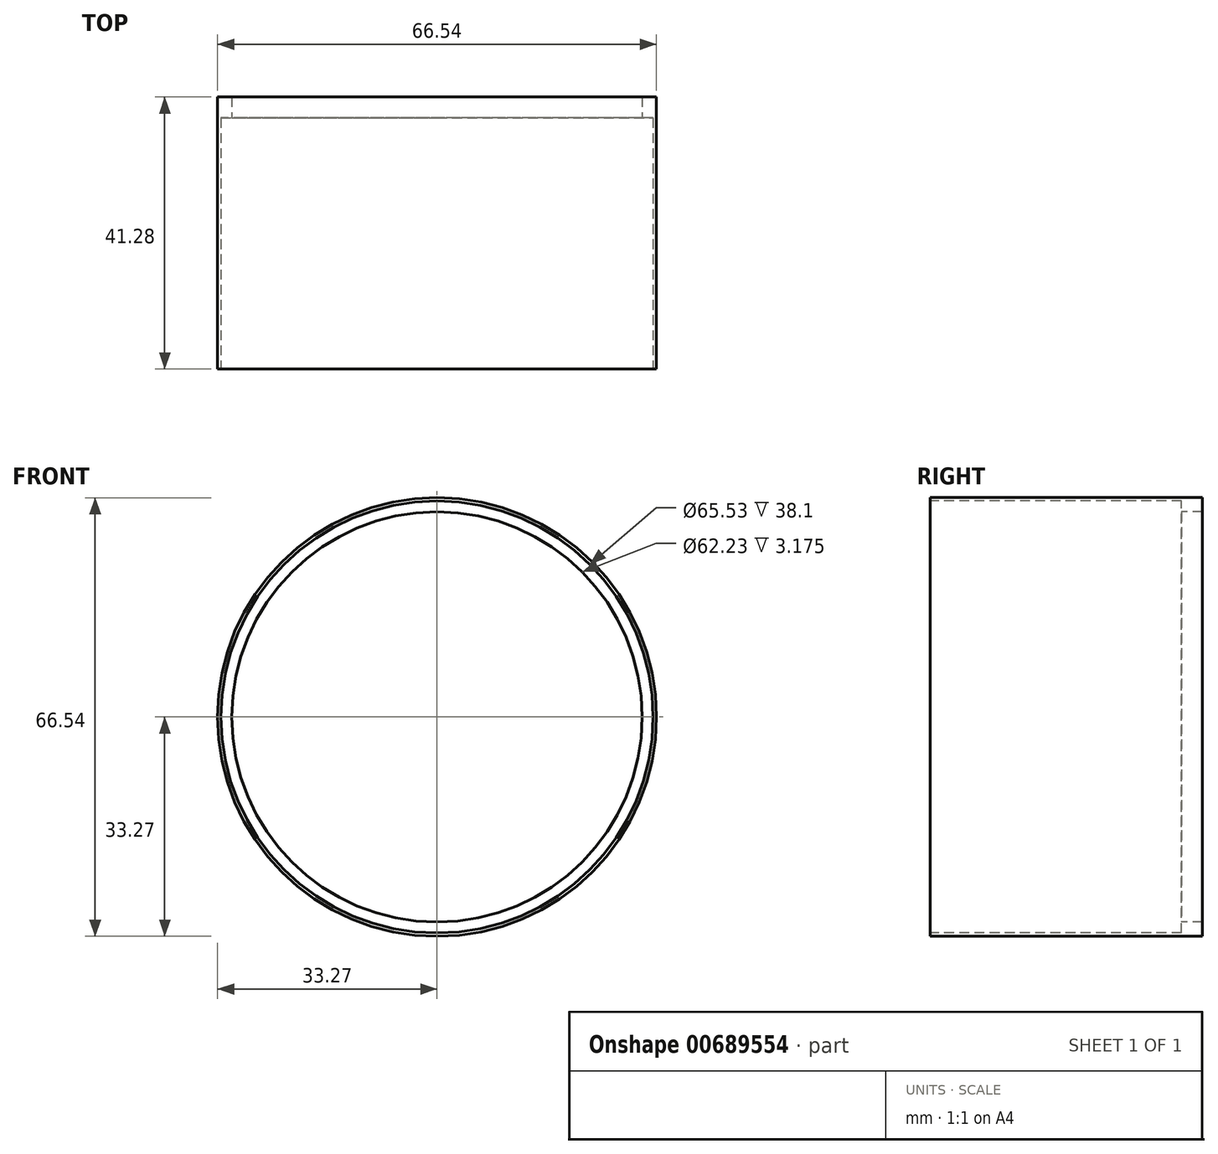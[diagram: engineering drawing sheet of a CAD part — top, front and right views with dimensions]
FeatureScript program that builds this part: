
annotation { "Feature Type Name" : "Feature", "Feature Type Description" : "" }
export const myFeature = defineFeature(function(context is Context, id is Id, definition is map)
    precondition{}
    {
        {
            var Q0;
            Q0=qCreatedBy(makeId("Front.planeOp"),FACE);
            var sketch = newSketch(context, id + "F0", { "sketchPlane" : qUnion([Q0])});
            skCircle(sketch, "E0", {"center": v(0, 0) * mm, "radius": 32.77 * mm});
            skCircle(sketch, "E1", {"center": v(0, 0) * mm, "radius": 33.27 * mm});
            skSolve(sketch);
        }
        {
            var Q0;
            Q0 = qSketchRegion(id + "F0", true);
            extrude(context, id + "F1", {"entities" : qUnion([Q0]), "oppositeDirection" : true, "depth" : 38.1 * mm, "offsetDistance" : 25.4 * mm});
        }
        {
            var Q0;
            Q0=makeQuery(id+"F1.opExtrude","CAP_FACE",FACE,{"disambiguationData":[OSD([sQuery(id+"F0.wireOp",EDGE,"E0"),sQuery(id+"F0.wireOp",EDGE,"E1")])],"isStart":false});
            var sketch = newSketch(context, id + "F2", { "sketchPlane" : qUnion([Q0])});
            skCircle(sketch, "E2", {"center": v(0, 0) * mm, "radius": 33.27 * mm});
            skCircle(sketch, "E3", {"center": v(0, 0) * mm, "radius": 31.12 * mm});
            skSolve(sketch);
        }
        {
            var Q0;
            Q0 = qSketchRegion(id + "F2", true);
            extrude(context, id + "F3", {"entities" : qUnion([Q0]), "operationType" : NewBodyOperationType.ADD, "depth" : 3.17 * mm, "offsetDistance" : 25.4 * mm});
        }
    });
